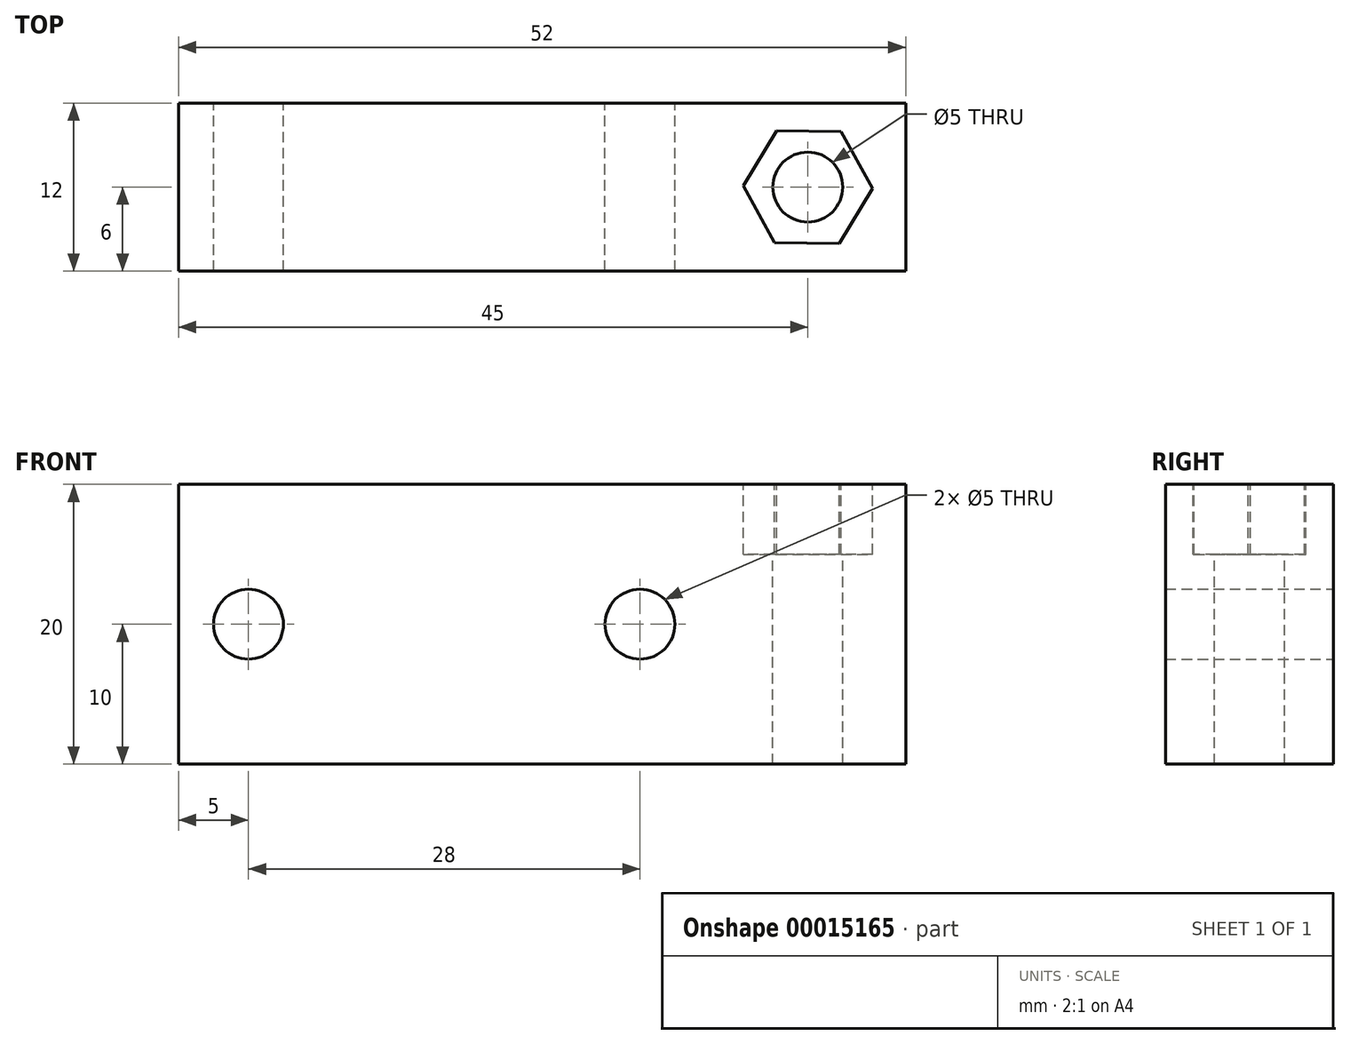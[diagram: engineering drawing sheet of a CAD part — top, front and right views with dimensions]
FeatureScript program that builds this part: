
annotation { "Feature Type Name" : "Feature", "Feature Type Description" : "" }
export const myFeature = defineFeature(function(context is Context, id is Id, definition is map)
    precondition{}
    {
        {
            var Q0;
            Q0=qCreatedBy(makeId("Front.planeOp"),FACE);
            var sketch = newSketch(context, id + "F0", { "sketchPlane" : qUnion([Q0])});
            skLineSegment(sketch, "E0.rect.bottom", {"start": v(26, 10) * mm, "end": v(-26, 10) * mm});
            skLineSegment(sketch, "E0.rect.top", {"start": v(26, -10) * mm, "end": v(-26, -10) * mm});
            skLineSegment(sketch, "E0.rect.left", {"start": v(26, 10) * mm, "end": v(26, -10) * mm});
            skLineSegment(sketch, "E0.rect.right", {"start": v(-26, 10) * mm, "end": v(-26, -10) * mm});
            skPoint(sketch, "E0.rect.middle", {"position": v(0, 0) * mm});
            skPoint(sketch, "E1", {"position": v(7, 0) * mm});
            skPoint(sketch, "E2", {"position": v(-21, 0) * mm});
            skSolve(sketch);
        }
        {
            var Q0;
            Q0=makeQuery(id+"F0.imprint","IMPRINT",FACE,{"disambiguationData":[TD([[makeQuery(id+"F0.imprint","IMPRINT",EDGE,{"derivedFrom":sQuery(id+"F0.wireOp",EDGE,"E0.rect.bottom")}),1.0]])]});
            extrude(context, id + "F1", {"entities" : qUnion([Q0]), "depth" : 12 * mm});
        }
        {
            var Q0;
            Q0=sQuery(id+"F0.wireOp",VERTEX,"E1");
            var Q1;
            Q1=sQuery(id+"F0.wireOp",VERTEX,"E2");
            var Q2;
            Q2=makeQuery(id+"F1.opExtrude","SWEPT_BODY",BODY,{"disambiguationData":[OSD([sQuery(id+"F0.wireOp",EDGE,"E0.rect.bottom"),sQuery(id+"F0.wireOp",EDGE,"E0.rect.top"),sQuery(id+"F0.wireOp",EDGE,"E0.rect.left"),sQuery(id+"F0.wireOp",EDGE,"E0.rect.right")])]});
            hole(context, id + "F2", {"style" : HoleStyle.SIMPLE, "holeDiameter" : 5 * mm, "endStyle" : HoleEndStyle.THROUGH, "oppositeDirection" : true, "locations" : qUnion([Q0, Q1]), "scope" : qUnion([Q2])});
        }
        {
            var Q0;
            Q0=makeQuery(id+"F1.opExtrude","SWEPT_FACE",FACE,{"disambiguationData":[OSD([sQuery(id+"F0.wireOp",EDGE,"E0.rect.bottom")])]});
            var sketch = newSketch(context, id + "F3", { "sketchPlane" : qUnion([Q0])});
            skPoint(sketch, "E3", {"position": v(19, -6) * mm});
            skCircle(sketch, "E4.cCircle", {"center": v(19, -6) * mm, "radius": 4 * mm, "construction": true});
            skLineSegment(sketch, "E4.0", {"start": v(23.62, -6.08) * mm, "end": v(21.24, -10.04) * mm});
            skLineSegment(sketch, "E4.1", {"start": v(21.24, -10.04) * mm, "end": v(16.62, -9.96) * mm});
            skLineSegment(sketch, "E4.2", {"start": v(16.62, -9.96) * mm, "end": v(14.38, -5.92) * mm});
            skLineSegment(sketch, "E4.3", {"start": v(14.38, -5.92) * mm, "end": v(16.76, -1.96) * mm});
            skLineSegment(sketch, "E4.4", {"start": v(16.76, -1.96) * mm, "end": v(21.38, -2.04) * mm});
            skLineSegment(sketch, "E4.5", {"start": v(21.38, -2.04) * mm, "end": v(23.62, -6.08) * mm});
            skPoint(sketch, "E4.0.midPoint", {"position": v(22.43, -8.06) * mm});
            skSolve(sketch);
        }
        {
            var Q0;
            Q0=sQuery(id+"F3.wireOp",VERTEX,"E3");
            var Q1;
            Q1=makeQuery(id+"F1.opExtrude","SWEPT_BODY",BODY,{"disambiguationData":[OSD([sQuery(id+"F0.wireOp",EDGE,"E0.rect.bottom"),sQuery(id+"F0.wireOp",EDGE,"E0.rect.top"),sQuery(id+"F0.wireOp",EDGE,"E0.rect.left"),sQuery(id+"F0.wireOp",EDGE,"E0.rect.right")])]});
            hole(context, id + "F4", {"style" : HoleStyle.SIMPLE, "holeDiameter" : 5 * mm, "endStyle" : HoleEndStyle.THROUGH, "locations" : qUnion([Q0]), "scope" : qUnion([Q1])});
        }
        {
            var Q0;
            Q0=makeQuery(id+"F3.imprint","IMPRINT",FACE,{"disambiguationData":[TD([[makeQuery(id+"F3.imprint","IMPRINT",EDGE,{"derivedFrom":sQuery(id+"F3.wireOp",EDGE,"E4.0")}),-1.0]])]});
            extrude(context, id + "F5", {"entities" : qUnion([Q0]), "operationType" : NewBodyOperationType.REMOVE, "oppositeDirection" : true, "depth" : 5 * mm});
        }
    });
